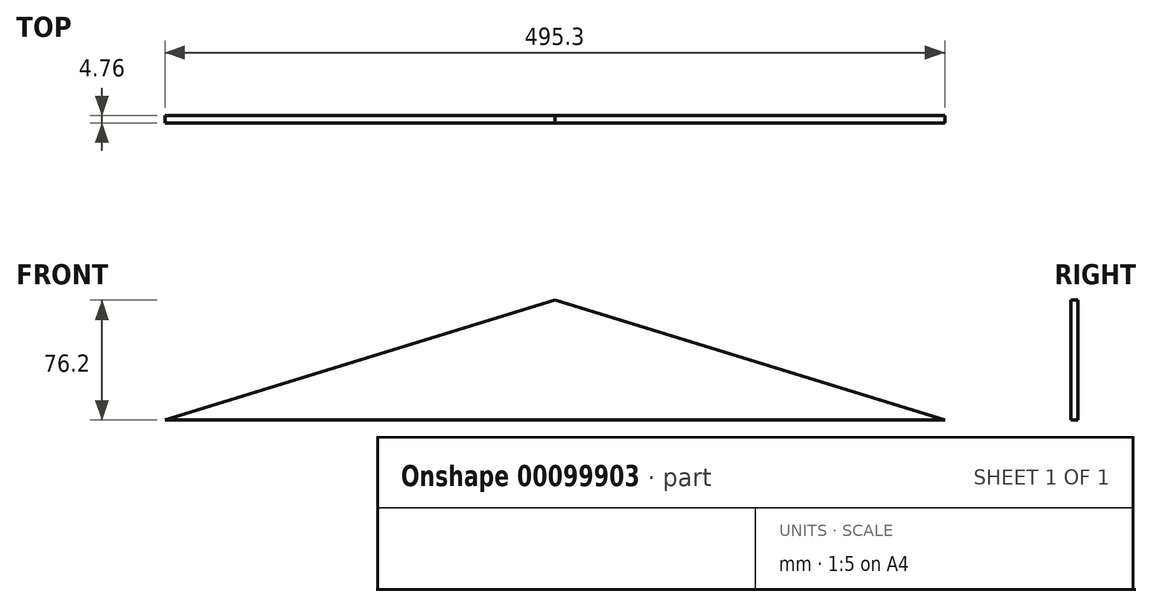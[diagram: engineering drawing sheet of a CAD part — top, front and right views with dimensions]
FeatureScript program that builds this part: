
annotation { "Feature Type Name" : "Feature", "Feature Type Description" : "" }
export const myFeature = defineFeature(function(context is Context, id is Id, definition is map)
    precondition{}
    {
        {
            var Q0;
            Q0=qCreatedBy(makeId("Front.planeOp"),FACE);
            var sketch = newSketch(context, id + "F0", { "sketchPlane" : qUnion([Q0])});
            skLineSegment(sketch, "E0", {"start": v(-239.52, 0) * mm, "end": v(255.78, 0) * mm});
            skLineSegment(sketch, "E1", {"start": v(8.13, 0) * mm, "end": v(8.13, 76.2) * mm});
            skLineSegment(sketch, "E2", {"start": v(-239.52, 0) * mm, "end": v(8.13, 76.2) * mm});
            skLineSegment(sketch, "E3", {"start": v(8.13, 76.2) * mm, "end": v(255.78, 0) * mm});
            skSolve(sketch);
        }
        {
            var Q0;
            Q0 = qSketchRegion(id + "F0", true);
            extrude(context, id + "F1", {"entities" : qUnion([Q0]), "depth" : 4.76 * mm});
        }
    });
